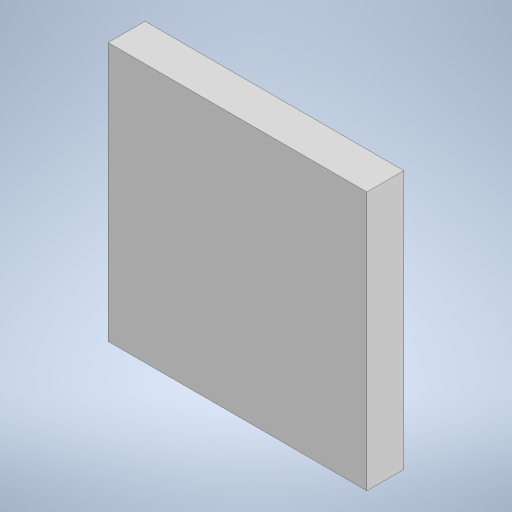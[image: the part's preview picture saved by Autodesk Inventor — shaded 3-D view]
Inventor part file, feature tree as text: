
AUTODESK INVENTOR PART (.ipt)
format: ipt  version: 2023 (Build 270158000, 158)  size: 237,056 bytes
history: native  units: in
note: dims shown in document units (in); Inventor stores cm internally (conversion verified against a paired STEP export)
features: extrude x1, sketch x1
ambient origin geometry x8: Origin, YZ Plane, XZ Plane, XY Plane, X Axis, Y Axis, Z Axis, Center Point
bodies: Solid1 (feature_tree)
feature tree (2):
  extrude  "Extrusion1"  Depth=1.378in
  sketch  "Sketch1"  dims[d0=1.378in d1=1.378in d2=0.1969in d3=0.0in]
